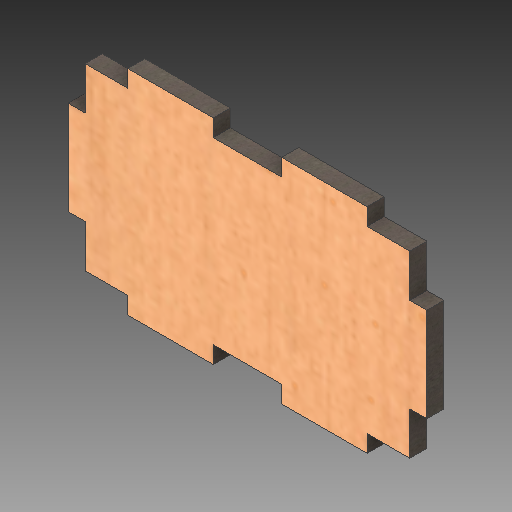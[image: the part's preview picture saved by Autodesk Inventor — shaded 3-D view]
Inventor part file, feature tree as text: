
AUTODESK INVENTOR PART (.ipt)
format: ipt  version: 2019 (Build 230136000, 136)  size: 236,544 bytes
history: native  units: mm
features: other x1, extrude x1, sketch x1
ambient origin geometry x8: Origin, YZ Plane, XZ Plane, XY Plane, X Axis, Y Axis, Z Axis, Center Point
bodies: Body1 (feature_tree)
feature tree (3):
  other  "Твердое тело1"
  extrude  "Выдавливание1"  Depth=20.0mm
  sketch  "Эскиз1"
